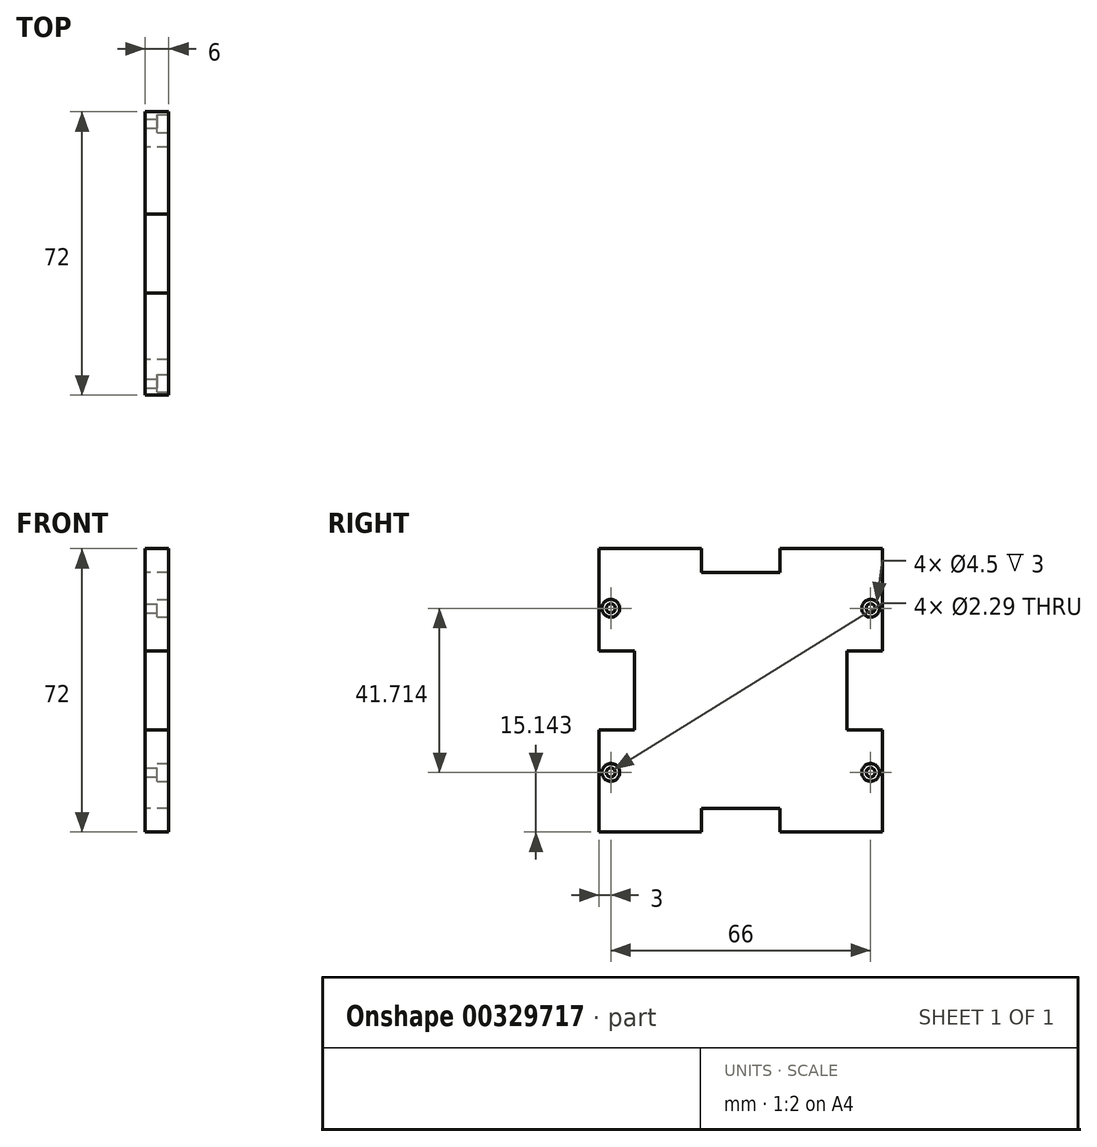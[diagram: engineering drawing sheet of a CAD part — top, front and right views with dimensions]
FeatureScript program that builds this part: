
annotation { "Feature Type Name" : "Feature", "Feature Type Description" : "" }
export const myFeature = defineFeature(function(context is Context, id is Id, definition is map)
    precondition{}
    {
        {
            var Q0;
            Q0=qCreatedBy(makeId("Right.planeOp"),FACE);
            var sketch = newSketch(context, id + "F0", { "sketchPlane" : qUnion([Q0])});
            skLineSegment(sketch, "E0.bottom", {"start": v(-36, -36) * mm, "end": v(36, -36) * mm});
            skLineSegment(sketch, "E0.top", {"start": v(-36, 36) * mm, "end": v(36, 36) * mm});
            skLineSegment(sketch, "E0.left", {"start": v(-36, -36) * mm, "end": v(-36, 36) * mm});
            skLineSegment(sketch, "E0.right", {"start": v(36, -36) * mm, "end": v(36, 36) * mm});
            skPoint(sketch, "E0.middle", {"position": v(0, 0) * mm});
            skLineSegment(sketch, "E1", {"start": v(0, 36) * mm, "end": v(0, -36) * mm, "construction": true});
            skLineSegment(sketch, "E2", {"start": v(-36, 0) * mm, "end": v(36, 0) * mm, "construction": true});
            skLineSegment(sketch, "E3", {"start": v(-36, 10) * mm, "end": v(-27, 10) * mm});
            skLineSegment(sketch, "E4", {"start": v(-27, 10) * mm, "end": v(-27, -10) * mm});
            skLineSegment(sketch, "E5", {"start": v(-27, -10) * mm, "end": v(-36, -10) * mm});
            skLineSegment(sketch, "E6.MirrorCS", {"start": v(36, 10) * mm, "end": v(27, 10) * mm});
            skLineSegment(sketch, "E7.MirrorCS", {"start": v(27, 10) * mm, "end": v(27, -10) * mm});
            skLineSegment(sketch, "E8.MirrorCS", {"start": v(27, -10) * mm, "end": v(36, -10) * mm});
            skLineSegment(sketch, "E9", {"start": v(-10, 36) * mm, "end": v(-10, 30) * mm});
            skLineSegment(sketch, "E10", {"start": v(-10, 30) * mm, "end": v(10, 30) * mm});
            skLineSegment(sketch, "E11", {"start": v(10, 30) * mm, "end": v(10, 36) * mm});
            skLineSegment(sketch, "E12.MirrorCS", {"start": v(10, -30) * mm, "end": v(10, -36) * mm});
            skLineSegment(sketch, "E13.MirrorCS", {"start": v(-10, -36) * mm, "end": v(-10, -30) * mm});
            skLineSegment(sketch, "E14.MirrorCS", {"start": v(0, -36) * mm, "end": v(0, 36) * mm, "construction": true});
            skLineSegment(sketch, "E15.MirrorCS", {"start": v(-10, -30) * mm, "end": v(10, -30) * mm});
            skSolve(sketch);
        }
        {
            var Q0;
            Q0=qSketchRegion(id+"F0",true);
            extrude(context, id + "F1", {"entities" : qUnion([Q0]), "depth" : 6 * mm});
        }
        {
            var Q0;
            {var subQ0=sQuery(id+"F0.wireOp",EDGE,"E9");Q0=makeQuery(id+"F0.imprint","IMPRINT",FACE,{"disambiguationData":[TD([[makeQuery(id+"F0.imprint","IMPRINT",EDGE,{"derivedFrom":subQ0}),1.0]])]});}
            var Q1;
            {var subQ0=sQuery(id+"F0.wireOp",EDGE,"E6.MirrorCS");Q1=makeQuery(id+"F0.imprint","IMPRINT",FACE,{"disambiguationData":[TD([[makeQuery(id+"F0.imprint","IMPRINT",EDGE,{"derivedFrom":subQ0}),1.0]])]});}
            var Q2;
            {var subQ0=sQuery(id+"F0.wireOp",EDGE,"E12.MirrorCS");Q2=makeQuery(id+"F0.imprint","IMPRINT",FACE,{"disambiguationData":[TD([[makeQuery(id+"F0.imprint","IMPRINT",EDGE,{"derivedFrom":subQ0}),-1.0]])]});}
            var Q3;
            {var subQ0=sQuery(id+"F0.wireOp",EDGE,"E3");Q3=makeQuery(id+"F0.imprint","IMPRINT",FACE,{"disambiguationData":[TD([[makeQuery(id+"F0.imprint","IMPRINT",EDGE,{"derivedFrom":subQ0}),-1.0]])]});}
            extrude(context, id + "F2", {"entities" : qUnion([Q0, Q1, Q2, Q3]), "operationType" : NewBodyOperationType.REMOVE, "endBound" : BoundingType.UP_TO_NEXT, "depth" : 25 * mm});
        }
        {
            var Q0;
            Q0=makeQuery(id+"F1.opExtrude","CAP_FACE",FACE,{"disambiguationData":[OSD([sQuery(id+"F0.wireOp",EDGE,"E0.top"),sQuery(id+"F0.wireOp",EDGE,"E0.left"),sQuery(id+"F0.wireOp",EDGE,"E0.right"),sQuery(id+"F0.wireOp",EDGE,"E0.bottom")])],"isStart":false});
            var sketch = newSketch(context, id + "F3", { "sketchPlane" : qUnion([Q0])});
            skCircle(sketch, "E16", {"center": v(-33, 20.86) * mm, "radius": 2.25 * mm});
            skCircle(sketch, "E17.MirrorC", {"center": v(-33, -20.86) * mm, "radius": 2.25 * mm});
            skCircle(sketch, "E18.MirrorC", {"center": v(33, 20.86) * mm, "radius": 2.25 * mm});
            skCircle(sketch, "E19.MirrorC", {"center": v(33, -20.86) * mm, "radius": 2.25 * mm});
            skCircle(sketch, "E20", {"center": v(-33, 20.86) * mm, "radius": 1.14 * mm});
            skCircle(sketch, "E21.MirrorC", {"center": v(33, 20.86) * mm, "radius": 1.14 * mm});
            skCircle(sketch, "E22.MirrorC", {"center": v(33, -20.86) * mm, "radius": 1.14 * mm});
            skCircle(sketch, "E23.MirrorC", {"center": v(-33, -20.86) * mm, "radius": 1.14 * mm});
            skSolve(sketch);
        }
        {
            var Q0;
            Q0=qSketchRegion(id+"F3",true);
            extrude(context, id + "F4", {"entities" : qUnion([Q0]), "operationType" : NewBodyOperationType.REMOVE, "oppositeDirection" : true, "depth" : 3 * mm});
        }
        {
            var Q0;
            Q0=makeQuery(id+"F4.boolean.opBoolean","SPLIT",FACE,{"disambiguationData":[TD([makeQuery(id+"F4.opExtrude","SWEPT_FACE",FACE,{"disambiguationData":[OSD([sQuery(id+"F3.wireOp",EDGE,"E20")])]})])],"derivedFrom":makeQuery(id+"F1.opExtrude","CAP_FACE",FACE,{"disambiguationData":[OSD([sQuery(id+"F0.wireOp",EDGE,"E0.top"),sQuery(id+"F0.wireOp",EDGE,"E0.left"),sQuery(id+"F0.wireOp",EDGE,"E0.right"),sQuery(id+"F0.wireOp",EDGE,"E0.bottom")])],"isStart":false})});
            var Q1;
            Q1=makeQuery(id+"F4.boolean.opBoolean","SPLIT",FACE,{"disambiguationData":[TD([makeQuery(id+"F4.opExtrude","SWEPT_FACE",FACE,{"disambiguationData":[OSD([sQuery(id+"F3.wireOp",EDGE,"E21.MirrorC")])]})])],"derivedFrom":makeQuery(id+"F1.opExtrude","CAP_FACE",FACE,{"disambiguationData":[OSD([sQuery(id+"F0.wireOp",EDGE,"E0.top"),sQuery(id+"F0.wireOp",EDGE,"E0.left"),sQuery(id+"F0.wireOp",EDGE,"E0.right"),sQuery(id+"F0.wireOp",EDGE,"E0.bottom")])],"isStart":false})});
            var Q2;
            Q2=makeQuery(id+"F4.boolean.opBoolean","SPLIT",FACE,{"disambiguationData":[TD([makeQuery(id+"F4.opExtrude","SWEPT_FACE",FACE,{"disambiguationData":[OSD([sQuery(id+"F3.wireOp",EDGE,"E22.MirrorC")])]})])],"derivedFrom":makeQuery(id+"F1.opExtrude","CAP_FACE",FACE,{"disambiguationData":[OSD([sQuery(id+"F0.wireOp",EDGE,"E0.top"),sQuery(id+"F0.wireOp",EDGE,"E0.left"),sQuery(id+"F0.wireOp",EDGE,"E0.right"),sQuery(id+"F0.wireOp",EDGE,"E0.bottom")])],"isStart":false})});
            var Q3;
            Q3=makeQuery(id+"F4.boolean.opBoolean","SPLIT",FACE,{"disambiguationData":[TD([makeQuery(id+"F4.opExtrude","SWEPT_FACE",FACE,{"disambiguationData":[OSD([sQuery(id+"F3.wireOp",EDGE,"E23.MirrorC")])]})])],"derivedFrom":makeQuery(id+"F1.opExtrude","CAP_FACE",FACE,{"disambiguationData":[OSD([sQuery(id+"F0.wireOp",EDGE,"E0.top"),sQuery(id+"F0.wireOp",EDGE,"E0.left"),sQuery(id+"F0.wireOp",EDGE,"E0.right"),sQuery(id+"F0.wireOp",EDGE,"E0.bottom")])],"isStart":false})});
            extrude(context, id + "F5", {"entities" : qUnion([Q0, Q1, Q2, Q3]), "operationType" : NewBodyOperationType.REMOVE, "endBound" : BoundingType.THROUGH_ALL, "oppositeDirection" : true, "depth" : 25 * mm});
        }
    });
